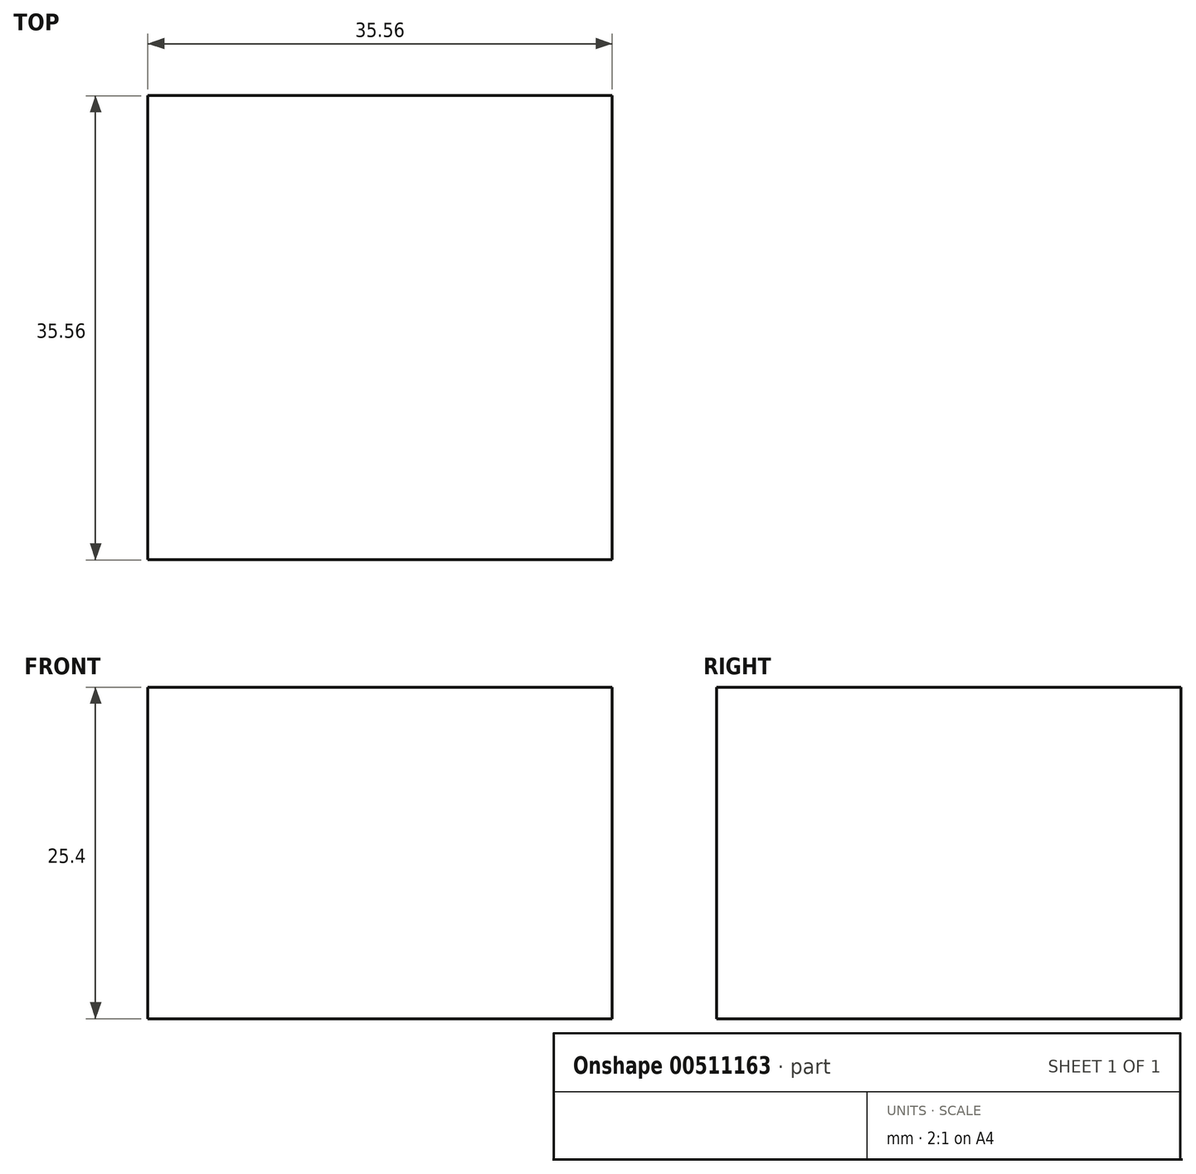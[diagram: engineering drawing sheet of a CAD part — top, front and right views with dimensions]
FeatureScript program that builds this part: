
annotation { "Feature Type Name" : "Feature", "Feature Type Description" : "" }
export const myFeature = defineFeature(function(context is Context, id is Id, definition is map)
    precondition{}
    {
        {
            var Q0;
            Q0=qCreatedBy(makeId("Top.planeOp"),FACE);
            var sketch = newSketch(context, id + "F0", { "sketchPlane" : qUnion([Q0])});
            skLineSegment(sketch, "E0", {"start": v(-19.24, 19.1) * mm, "end": v(-19.24, -16.47) * mm});
            skLineSegment(sketch, "E1", {"start": v(-19.24, -16.47) * mm, "end": v(16.32, -16.47) * mm});
            skLineSegment(sketch, "E2", {"start": v(16.32, -16.47) * mm, "end": v(16.32, 19.1) * mm});
            skLineSegment(sketch, "E3", {"start": v(17.2, 19.1) * mm, "end": v(-19.24, 19.1) * mm});
            skSolve(sketch);
        }
        {
            var Q0;
            {var subQ0=sQuery(id+"F0.wireOp",EDGE,"E0");Q0=makeQuery(id+"F0.imprint","IMPRINT",FACE,{"disambiguationData":[TD([[makeQuery(id+"F0.imprint","IMPRINT",EDGE,{"derivedFrom":subQ0}),1.0]])]});}
            extrude(context, id + "F1", {"entities" : qUnion([Q0]), "depth" : 25.4 * mm});
        }
    });
